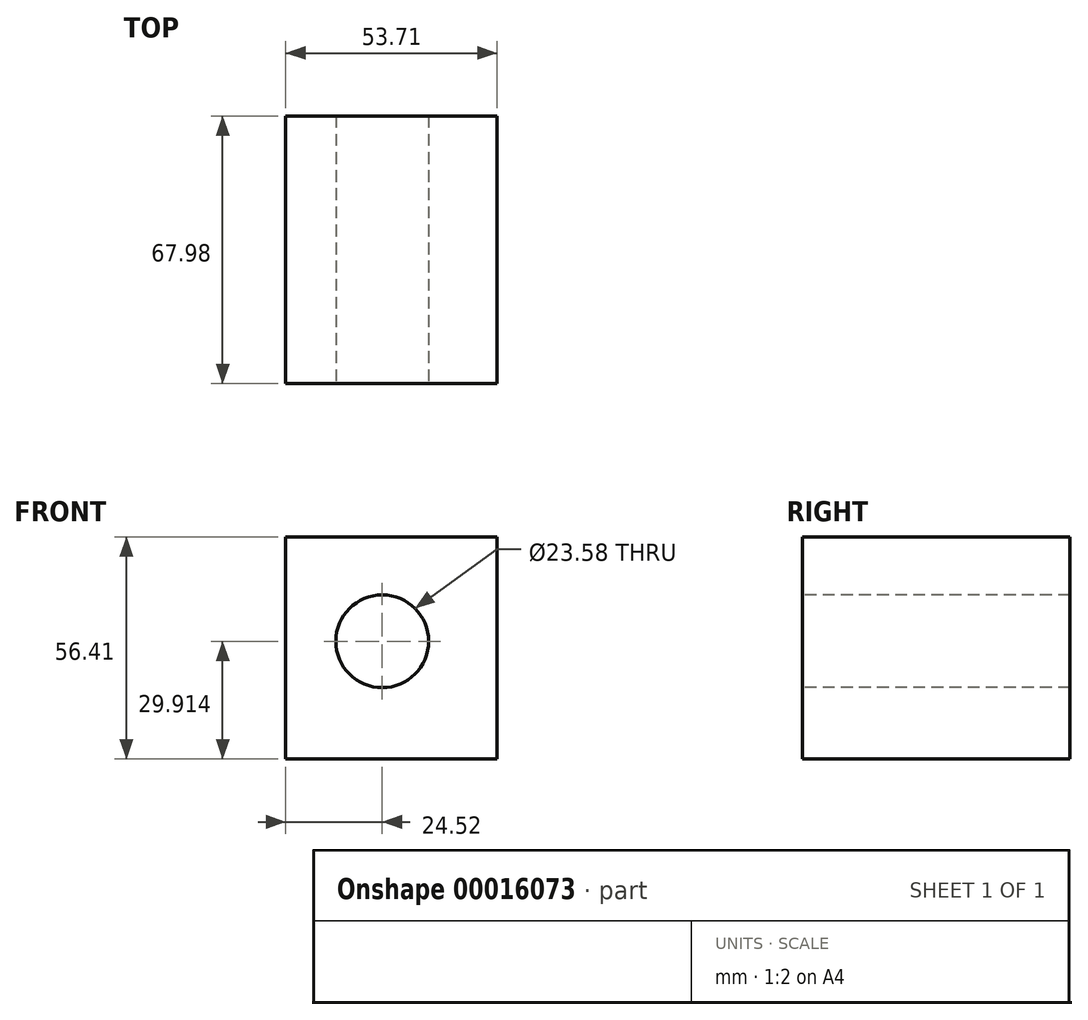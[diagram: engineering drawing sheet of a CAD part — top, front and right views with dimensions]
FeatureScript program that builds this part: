
annotation { "Feature Type Name" : "Feature", "Feature Type Description" : "" }
export const myFeature = defineFeature(function(context is Context, id is Id, definition is map)
    precondition{}
    {
        {
            var Q0;
            Q0=qCreatedBy(makeId("Top.planeOp"),FACE);
            var sketch = newSketch(context, id + "F0", { "sketchPlane" : qUnion([Q0])});
            skLineSegment(sketch, "E0.bottom", {"start": v(0, 0) * mm, "end": v(53.7, 0) * mm});
            skLineSegment(sketch, "E0.top", {"start": v(0, -67.98) * mm, "end": v(53.7, -67.98) * mm});
            skLineSegment(sketch, "E0.left", {"start": v(0, 0) * mm, "end": v(0, -67.98) * mm});
            skLineSegment(sketch, "E0.right", {"start": v(53.7, 0) * mm, "end": v(53.7, -67.98) * mm});
            skSolve(sketch);
        }
        {
            var Q0;
            Q0 = qSketchRegion(id + "F0", true);
            extrude(context, id + "F1", {"entities" : qUnion([Q0]), "depth" : 56.4 * mm});
        }
        {
            var Q0;
            Q0=makeQuery(id+"F1.opExtrude","SWEPT_FACE",FACE,{"disambiguationData":[OSD([sQuery(id+"F0.wireOp",EDGE,"E0.top")])]});
            var sketch = newSketch(context, id + "F2", { "sketchPlane" : qUnion([Q0])});
            skCircle(sketch, "E1", {"center": v(24.52, 29.91) * mm, "radius": 11.79 * mm});
            skSolve(sketch);
        }
        {
            var Q0;
            Q0 = qSketchRegion(id + "F2", true);
            extrude(context, id + "F3", {"entities" : qUnion([Q0]), "operationType" : NewBodyOperationType.REMOVE, "endBound" : BoundingType.THROUGH_ALL, "oppositeDirection" : true, "depth" : 120.73 * mm});
        }
    });
